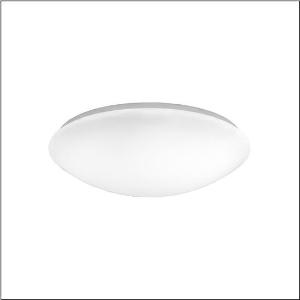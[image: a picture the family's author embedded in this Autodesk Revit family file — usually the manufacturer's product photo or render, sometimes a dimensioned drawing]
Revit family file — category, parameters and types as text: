
# Revit family: round_31_b_5pja210001a
name_source: partatom
category: Lighting Fixtures
units: mm (PartAtom-declared; Revit-internal decimal feet)

## family parameters
Cut with Voids When Loaded = No
Host = Face
Light Source = No
Part Type = Normal
Room Calculation Point = No
Round Connector Dimension = Use Diameter
Shared = No

## types (1)
- --- (1 x LED, 4700 lm, 39 W, 3000K)
    Apparent Load = 39 VA
    CIE Flux Codes = 42 71 89 88 100
    Color Rendering = 80
    Color Temperature = 3000K
    Default Elevation = 1800 mm
    Description = Round 31 B, wall and ceiling luminaire, primary optical cover: enclosure, of PMMA, light emission: direct distribution, primary light characteristic: symmetric, installation type: surface-mounted, LED, rated luminous flux: 4.700lm, luminous efficacy: 121lm/W, light colour: 830, colour temperature: 3000K, with terminal, 3-pole, max. 2.5mm², mains connection: 230V, AC, 50/60Hz, rated input power: 39W, luminaire housing, round, of steel, white, diameter: 464mm, height: 120mm, protection rating (complete): IP40, insulation class (complete): insulation class I (protective earthing), certification: CE, impact resistance: IK02, permissible operating ambient temperature: -20..+25°C, packaging unit: 1 piece
    Height = 120 mm
    Lamp = 1 x LED
    Lamp Light Flux = 4700 lm
    Lamp Power = 39 W
    Lamp count = 1
    Length = 464 mm
    Luminous efficacy = 121 lm/W
    Manufacturer = Siteco
    ModVariant = No
    Model = 5PJA210001A
    Mounting Place = Ceiling
    Mounting Type = Surface mounted
    Number of Poles = 1
    OnlyDefault = Yes
    Power Factor = 1
    Product Name = Round 31 B
    Product group = wall and ceiling luminaire
    ProductGroupID = 301
    Protection Class = Protection class I
    Protection Degree = IP 40
    RLX_Detail_Level = 1
    RLX_Emergency_Light_Flux = 0 lm
    RLX_Emergency_Type = 0
    RLX_Emergency_Type_DB = No
    RlxData = <blob elided: 13793 chars, md5=76071228>
    Socket = socket
    Standby Power = 0 W
    System Light Flux = 4700 lm
    System Power = 39 W
    Type Comments = factory setting: luminous flux: 100 % | (ON | ON | ON) | 1050 mA
    Type Image = l_1258313.jpg
    URL = http://relux.com
    VarID = @adj_013713
    Voltage = 0 V
    Weight = 0.00 kg
    Width = 0 mm  [stored 0 ft]

note: [stored X ft] marks values corroborated as IEEE doubles in the binary element streams (Revit-internal decimal feet)

## geometry (parser evidence)
native form markers: Sweep x11
no freeform markers — native parametric forms only
